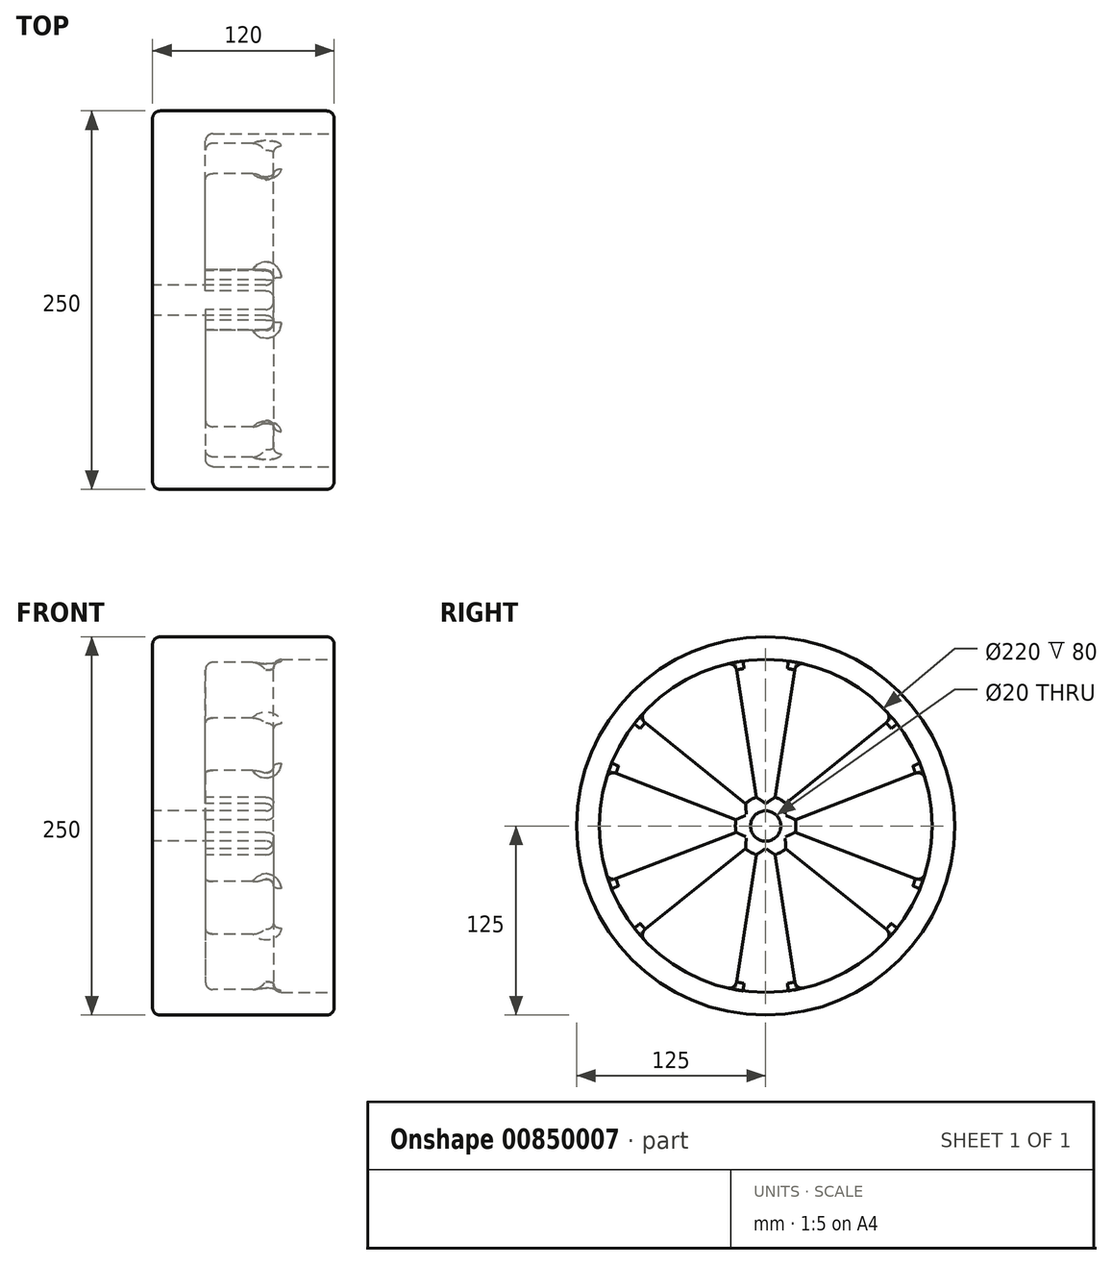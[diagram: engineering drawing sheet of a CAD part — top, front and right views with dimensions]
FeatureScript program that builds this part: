
annotation { "Feature Type Name" : "Feature", "Feature Type Description" : "" }
export const myFeature = defineFeature(function(context is Context, id is Id, definition is map)
    precondition{}
    {
        {
            var Q0;
            Q0=qCreatedBy(makeId("Right.planeOp"),FACE);
            var sketch = newSketch(context, id + "F0", { "sketchPlane" : qUnion([Q0])});
            skCircle(sketch, "E0", {"center": v(0, 0) * mm, "radius": 125 * mm});
            skSolve(sketch);
        }
        {
            var Q0;
            Q0=makeQuery(id+"F0.imprint","IMPRINT",FACE,{"disambiguationData":[TD([[makeQuery(id+"F0.imprint","IMPRINT",EDGE,{"derivedFrom":sQuery(id+"F0.wireOp",EDGE,"E0")}),1.0]])]});
            extrude(context, id + "F1", {"entities" : qUnion([Q0]), "depth" : 120 * mm, "offsetDistance" : 25 * mm});
        }
        {
            var Q0;
            Q0=makeQuery(id+"F1.opExtrude","CAP_FACE",FACE,{"disambiguationData":[OSD([sQuery(id+"F0.wireOp",EDGE,"E0")])],"isStart":false});
            var sketch = newSketch(context, id + "F2", { "sketchPlane" : qUnion([Q0])});
            skCircle(sketch, "E1", {"center": v(0, 0) * mm, "radius": 110 * mm});
            skSolve(sketch);
        }
        {
            var Q0;
            Q0=makeQuery(id+"F2.imprint","IMPRINT",FACE,{"disambiguationData":[TD([[makeQuery(id+"F2.imprint","IMPRINT",EDGE,{"derivedFrom":sQuery(id+"F2.wireOp",EDGE,"E1")}),1.0]])]});
            extrude(context, id + "F3", {"entities" : qUnion([Q0]), "operationType" : NewBodyOperationType.REMOVE, "oppositeDirection" : true, "depth" : 60 * mm, "offsetDistance" : 25 * mm});
        }
        {
            var Q0;
            Q0=makeQuery(id+"F3.boolean.opBoolean","COPY",FACE,{"derivedFrom":makeQuery(id+"F3.opExtrude","CAP_FACE",FACE,{"disambiguationData":[OSD([sQuery(id+"F2.wireOp",EDGE,"E1")])],"isStart":false})});
            var sketch = newSketch(context, id + "F4", { "sketchPlane" : qUnion([Q0])});
            skCircle(sketch, "E2", {"center": v(0, 0) * mm, "radius": 20 * mm});
            skCircle(sketch, "E3", {"center": v(0, 0) * mm, "radius": 10 * mm});
            skLineSegment(sketch, "E4", {"start": v(-6.24, 19) * mm, "end": v(-20, 108.17) * mm});
            skLineSegment(sketch, "E5", {"start": v(6.24, 19) * mm, "end": v(20, 108.17) * mm});
            skLineSegment(sketch, "E6.1.0", {"start": v(-13.33, 14.9) * mm, "end": v(-83.67, 71.4) * mm});
            skLineSegment(sketch, "E6.1.1", {"start": v(-19.58, 4.1) * mm, "end": v(-103.67, 36.76) * mm});
            skLineSegment(sketch, "E6.2.0", {"start": v(-19.58, -4.1) * mm, "end": v(-103.67, -36.76) * mm});
            skLineSegment(sketch, "E6.2.1", {"start": v(-13.33, -14.9) * mm, "end": v(-83.67, -71.4) * mm});
            skLineSegment(sketch, "E6.3.0", {"start": v(-6.24, -19) * mm, "end": v(-20, -108.17) * mm});
            skLineSegment(sketch, "E6.3.1", {"start": v(6.24, -19) * mm, "end": v(20, -108.17) * mm});
            skLineSegment(sketch, "E6.4.0", {"start": v(13.33, -14.9) * mm, "end": v(83.67, -71.4) * mm});
            skLineSegment(sketch, "E6.4.1", {"start": v(19.58, -4.1) * mm, "end": v(103.67, -36.76) * mm});
            skLineSegment(sketch, "E6.5.0", {"start": v(19.58, 4.1) * mm, "end": v(103.67, 36.76) * mm});
            skLineSegment(sketch, "E6.5.1", {"start": v(13.33, 14.9) * mm, "end": v(83.67, 71.4) * mm});
            skSolve(sketch);
        }
        {
            var Q0;
            {var subQ0=sQuery(id+"F4.wireOp",EDGE,"E4");Q0=makeQuery(id+"F4.imprint","IMPRINT",FACE,{"disambiguationData":[TD([[makeQuery(id+"F4.imprint","IMPRINT",EDGE,{"derivedFrom":subQ0}),-1.0]])]});}
            var Q1;
            Q1=makeQuery(id+"F4.imprint","IMPRINT",FACE,{"disambiguationData":[TD([[makeQuery(id+"F4.imprint","IMPRINT",EDGE,{"derivedFrom":sQuery(id+"F4.wireOp",EDGE,"E3")}),-1.0]])]});
            var Q2;
            {var subQ0=sQuery(id+"F4.wireOp",EDGE,"E6.5.0");Q2=makeQuery(id+"F4.imprint","IMPRINT",FACE,{"disambiguationData":[TD([[makeQuery(id+"F4.imprint","IMPRINT",EDGE,{"derivedFrom":subQ0}),1.0]])]});}
            var Q3;
            {var subQ0=sQuery(id+"F4.wireOp",EDGE,"E6.4.0");Q3=makeQuery(id+"F4.imprint","IMPRINT",FACE,{"disambiguationData":[TD([[makeQuery(id+"F4.imprint","IMPRINT",EDGE,{"derivedFrom":subQ0}),1.0]])]});}
            var Q4;
            {var subQ0=sQuery(id+"F4.wireOp",EDGE,"E6.3.0");Q4=makeQuery(id+"F4.imprint","IMPRINT",FACE,{"disambiguationData":[TD([[makeQuery(id+"F4.imprint","IMPRINT",EDGE,{"derivedFrom":subQ0}),1.0]])]});}
            var Q5;
            {var subQ0=sQuery(id+"F4.wireOp",EDGE,"E6.2.0");Q5=makeQuery(id+"F4.imprint","IMPRINT",FACE,{"disambiguationData":[TD([[makeQuery(id+"F4.imprint","IMPRINT",EDGE,{"derivedFrom":subQ0}),1.0]])]});}
            var Q6;
            {var subQ0=sQuery(id+"F4.wireOp",EDGE,"E6.1.0");Q6=makeQuery(id+"F4.imprint","IMPRINT",FACE,{"disambiguationData":[TD([[makeQuery(id+"F4.imprint","IMPRINT",EDGE,{"derivedFrom":subQ0}),1.0]])]});}
            extrude(context, id + "F5", {"entities" : qUnion([Q0, Q1, Q2, Q3, Q4, Q5, Q6]), "operationType" : NewBodyOperationType.ADD, "depth" : 20 * mm, "offsetDistance" : 25 * mm});
        }
        {
            var Q0;
            Q0=makeQuery(id+"F5.boolean.opBoolean","SPLIT",FACE,{"disambiguationData":[TD([makeQuery(id+"F5.opExtrude","SWEPT_FACE",FACE,{"disambiguationData":[OSD([sQuery(id+"F4.wireOp",EDGE,"E3")])]})])],"derivedFrom":makeQuery(id+"F3.boolean.opBoolean","COPY",FACE,{"derivedFrom":makeQuery(id+"F3.opExtrude","CAP_FACE",FACE,{"disambiguationData":[OSD([sQuery(id+"F2.wireOp",EDGE,"E1")])],"isStart":false})})});
            extrude(context, id + "F6", {"entities" : qUnion([Q0]), "operationType" : NewBodyOperationType.REMOVE, "oppositeDirection" : true, "depth" : 60 * mm, "offsetDistance" : 25 * mm});
        }
        {
            var Q0;
            {var subQ0=sQuery(id+"F2.wireOp",EDGE,"E1");var subQ1=sQuery(id+"F4.wireOp",EDGE,"E6.4.1");Q0=makeQuery(id+"F5.boolean.opBoolean","SPLIT",FACE,{"disambiguationData":[TD([makeQuery(id+"F5.opExtrude","SWEPT_FACE",FACE,{"disambiguationData":[OSD([subQ1])]})])],"derivedFrom":makeQuery(id+"F3.boolean.opBoolean","COPY",FACE,{"derivedFrom":makeQuery(id+"F3.opExtrude","CAP_FACE",FACE,{"disambiguationData":[OSD([subQ0])],"isStart":false})})});}
            var Q1;
            {var subQ0=sQuery(id+"F2.wireOp",EDGE,"E1");var subQ1=sQuery(id+"F4.wireOp",EDGE,"E5");Q1=makeQuery(id+"F5.boolean.opBoolean","SPLIT",FACE,{"disambiguationData":[TD([makeQuery(id+"F5.opExtrude","SWEPT_FACE",FACE,{"disambiguationData":[OSD([subQ1])]})])],"derivedFrom":makeQuery(id+"F3.boolean.opBoolean","COPY",FACE,{"derivedFrom":makeQuery(id+"F3.opExtrude","CAP_FACE",FACE,{"disambiguationData":[OSD([subQ0])],"isStart":false})})});}
            var Q2;
            {var subQ0=sQuery(id+"F2.wireOp",EDGE,"E1");var subQ1=sQuery(id+"F4.wireOp",EDGE,"E4");Q2=makeQuery(id+"F5.boolean.opBoolean","SPLIT",FACE,{"disambiguationData":[TD([makeQuery(id+"F5.opExtrude","SWEPT_FACE",FACE,{"disambiguationData":[OSD([subQ1])]})])],"derivedFrom":makeQuery(id+"F3.boolean.opBoolean","COPY",FACE,{"derivedFrom":makeQuery(id+"F3.opExtrude","CAP_FACE",FACE,{"disambiguationData":[OSD([subQ0])],"isStart":false})})});}
            var Q3;
            {var subQ0=sQuery(id+"F2.wireOp",EDGE,"E1");var subQ1=sQuery(id+"F4.wireOp",EDGE,"E6.1.1");Q3=makeQuery(id+"F5.boolean.opBoolean","SPLIT",FACE,{"disambiguationData":[TD([makeQuery(id+"F5.opExtrude","SWEPT_FACE",FACE,{"disambiguationData":[OSD([subQ1])]})])],"derivedFrom":makeQuery(id+"F3.boolean.opBoolean","COPY",FACE,{"derivedFrom":makeQuery(id+"F3.opExtrude","CAP_FACE",FACE,{"disambiguationData":[OSD([subQ0])],"isStart":false})})});}
            var Q4;
            {var subQ0=sQuery(id+"F2.wireOp",EDGE,"E1");var subQ1=sQuery(id+"F4.wireOp",EDGE,"E6.2.1");Q4=makeQuery(id+"F5.boolean.opBoolean","SPLIT",FACE,{"disambiguationData":[TD([makeQuery(id+"F5.opExtrude","SWEPT_FACE",FACE,{"disambiguationData":[OSD([subQ1])]})])],"derivedFrom":makeQuery(id+"F3.boolean.opBoolean","COPY",FACE,{"derivedFrom":makeQuery(id+"F3.opExtrude","CAP_FACE",FACE,{"disambiguationData":[OSD([subQ0])],"isStart":false})})});}
            var Q5;
            {var subQ0=sQuery(id+"F2.wireOp",EDGE,"E1");var subQ2=sQuery(id+"F4.wireOp",EDGE,"E6.3.1");Q5=makeQuery(id+"F5.boolean.opBoolean","SPLIT",FACE,{"disambiguationData":[TD([makeQuery(id+"F5.opExtrude","SWEPT_FACE",FACE,{"disambiguationData":[OSD([subQ2])]})])],"derivedFrom":makeQuery(id+"F3.boolean.opBoolean","COPY",FACE,{"derivedFrom":makeQuery(id+"F3.opExtrude","CAP_FACE",FACE,{"disambiguationData":[OSD([subQ0])],"isStart":false})})});}
            extrude(context, id + "F7", {"entities" : qUnion([Q0, Q1, Q2, Q3, Q4, Q5]), "operationType" : NewBodyOperationType.REMOVE, "oppositeDirection" : true, "depth" : 25 * mm, "offsetDistance" : 25 * mm});
        }
        {
            var Q0;
            Q0=makeQuery(id+"F3.boolean.opBoolean","COPY",EDGE,{"derivedFrom":makeQuery(id+"F3.opExtrude","CAP_EDGE",EDGE,{"disambiguationData":[OSD([sQuery(id+"F2.wireOp",EDGE,"E1")])],"isStart":true})});
            var Q1;
            Q1=makeQuery(id+"F1.opExtrude","CAP_EDGE",EDGE,{"disambiguationData":[OSD([sQuery(id+"F0.wireOp",EDGE,"E0")])],"isStart":false});
            var Q2;
            Q2=makeQuery(id+"F5.opExtrude","CAP_EDGE",EDGE,{"disambiguationData":[OSD([sQuery(id+"F4.wireOp",EDGE,"E6.1.1")])],"isStart":false});
            var Q3;
            Q3=makeQuery(id+"F5.opExtrude","CAP_EDGE",EDGE,{"disambiguationData":[OSD([sQuery(id+"F4.wireOp",EDGE,"E6.1.0")])],"isStart":false});
            var Q4;
            Q4=makeQuery(id+"F5.opExtrude","CAP_EDGE",EDGE,{"disambiguationData":[OSD([sQuery(id+"F4.wireOp",EDGE,"E4")])],"isStart":false});
            var Q5;
            Q5=makeQuery(id+"F5.opExtrude","CAP_EDGE",EDGE,{"disambiguationData":[OSD([sQuery(id+"F4.wireOp",EDGE,"E5")])],"isStart":false});
            var Q6;
            Q6=makeQuery(id+"F5.opExtrude","CAP_EDGE",EDGE,{"disambiguationData":[OSD([sQuery(id+"F4.wireOp",EDGE,"E6.5.1")])],"isStart":false});
            var Q7;
            Q7=makeQuery(id+"F5.opExtrude","CAP_EDGE",EDGE,{"disambiguationData":[OSD([sQuery(id+"F4.wireOp",EDGE,"E6.4.1")])],"isStart":false});
            var Q8;
            Q8=makeQuery(id+"F5.opExtrude","CAP_EDGE",EDGE,{"disambiguationData":[OSD([sQuery(id+"F4.wireOp",EDGE,"E6.4.0")])],"isStart":false});
            var Q9;
            Q9=makeQuery(id+"F5.opExtrude","CAP_EDGE",EDGE,{"disambiguationData":[OSD([sQuery(id+"F4.wireOp",EDGE,"E6.3.0")])],"isStart":false});
            var Q10;
            Q10=makeQuery(id+"F5.opExtrude","CAP_EDGE",EDGE,{"disambiguationData":[OSD([sQuery(id+"F4.wireOp",EDGE,"E6.2.0")])],"isStart":false});
            var Q11;
            Q11=makeQuery(id+"F5.opExtrude","CAP_EDGE",EDGE,{"disambiguationData":[OSD([sQuery(id+"F4.wireOp",EDGE,"E6.2.1")])],"isStart":false});
            var Q12;
            Q12=makeQuery(id+"F5.opExtrude","CAP_EDGE",EDGE,{"disambiguationData":[OSD([sQuery(id+"F4.wireOp",EDGE,"E6.3.1")])],"isStart":false});
            var Q13;
            Q13=makeQuery(id+"F5.opExtrude","CAP_EDGE",EDGE,{"disambiguationData":[OSD([sQuery(id+"F4.wireOp",EDGE,"E6.5.0")])],"isStart":false});
            var Q14;
            {var subQ0=sQuery(id+"F2.wireOp",EDGE,"E1");Q14=makeQuery(id+"F7.boolean.opBoolean","COPY",EDGE,{"derivedFrom":makeQuery(id+"F7.opExtrude","CAP_EDGE",EDGE,{"disambiguationData":[OSD([subQ0]),TDD([makeQuery(id+"F5.boolean.opBoolean","SPLIT",EDGE,{"disambiguationData":[TD([makeQuery(id+"F5.opExtrude","SWEPT_FACE",FACE,{"disambiguationData":[OSD([sQuery(id+"F4.wireOp",EDGE,"E6.1.1")])]})])],"derivedFrom":makeQuery(id+"F3.boolean.opBoolean","COPY",EDGE,{"derivedFrom":makeQuery(id+"F3.opExtrude","CAP_EDGE",EDGE,{"disambiguationData":[OSD([subQ0])],"isStart":false})})})])],"isStart":false})});}
            var Q15;
            {var subQ0=sQuery(id+"F2.wireOp",EDGE,"E1");Q15=makeQuery(id+"F7.boolean.opBoolean","COPY",EDGE,{"derivedFrom":makeQuery(id+"F7.opExtrude","CAP_EDGE",EDGE,{"disambiguationData":[OSD([subQ0]),TDD([makeQuery(id+"F5.boolean.opBoolean","SPLIT",EDGE,{"disambiguationData":[TD([makeQuery(id+"F5.opExtrude","SWEPT_FACE",FACE,{"disambiguationData":[OSD([sQuery(id+"F4.wireOp",EDGE,"E4")])]})])],"derivedFrom":makeQuery(id+"F3.boolean.opBoolean","COPY",EDGE,{"derivedFrom":makeQuery(id+"F3.opExtrude","CAP_EDGE",EDGE,{"disambiguationData":[OSD([subQ0])],"isStart":false})})})])],"isStart":false})});}
            var Q16;
            {var subQ0=sQuery(id+"F2.wireOp",EDGE,"E1");Q16=makeQuery(id+"F7.boolean.opBoolean","COPY",EDGE,{"derivedFrom":makeQuery(id+"F7.opExtrude","CAP_EDGE",EDGE,{"disambiguationData":[OSD([subQ0]),TDD([makeQuery(id+"F5.boolean.opBoolean","SPLIT",EDGE,{"disambiguationData":[TD([makeQuery(id+"F5.opExtrude","SWEPT_FACE",FACE,{"disambiguationData":[OSD([sQuery(id+"F4.wireOp",EDGE,"E5")])]})])],"derivedFrom":makeQuery(id+"F3.boolean.opBoolean","COPY",EDGE,{"derivedFrom":makeQuery(id+"F3.opExtrude","CAP_EDGE",EDGE,{"disambiguationData":[OSD([subQ0])],"isStart":false})})})])],"isStart":false})});}
            var Q17;
            {var subQ0=sQuery(id+"F2.wireOp",EDGE,"E1");Q17=makeQuery(id+"F7.boolean.opBoolean","COPY",EDGE,{"derivedFrom":makeQuery(id+"F7.opExtrude","CAP_EDGE",EDGE,{"disambiguationData":[OSD([subQ0]),TDD([makeQuery(id+"F5.boolean.opBoolean","SPLIT",EDGE,{"disambiguationData":[TD([makeQuery(id+"F5.opExtrude","SWEPT_FACE",FACE,{"disambiguationData":[OSD([sQuery(id+"F4.wireOp",EDGE,"E6.4.1")])]})])],"derivedFrom":makeQuery(id+"F3.boolean.opBoolean","COPY",EDGE,{"derivedFrom":makeQuery(id+"F3.opExtrude","CAP_EDGE",EDGE,{"disambiguationData":[OSD([subQ0])],"isStart":false})})})])],"isStart":false})});}
            var Q18;
            Q18=makeQuery(id+"F5.opExtrude","CAP_FACE",FACE,{"disambiguationData":[OSD([sQuery(id+"F2.wireOp",EDGE,"E1"),sQuery(id+"F4.wireOp",EDGE,"E2"),sQuery(id+"F4.wireOp",EDGE,"E3"),sQuery(id+"F4.wireOp",EDGE,"E4"),sQuery(id+"F4.wireOp",EDGE,"E5"),sQuery(id+"F4.wireOp",EDGE,"E6.1.0"),sQuery(id+"F4.wireOp",EDGE,"E6.1.1"),sQuery(id+"F4.wireOp",EDGE,"E6.2.0"),sQuery(id+"F4.wireOp",EDGE,"E6.2.1"),sQuery(id+"F4.wireOp",EDGE,"E6.3.0"),sQuery(id+"F4.wireOp",EDGE,"E6.3.1"),sQuery(id+"F4.wireOp",EDGE,"E6.4.0"),sQuery(id+"F4.wireOp",EDGE,"E6.4.1"),sQuery(id+"F4.wireOp",EDGE,"E6.5.0"),sQuery(id+"F4.wireOp",EDGE,"E6.5.1")])],"isStart":false});
            var Q19;
            {var subQ0=sQuery(id+"F2.wireOp",EDGE,"E1");Q19=makeQuery(id+"F7.boolean.opBoolean","COPY",EDGE,{"derivedFrom":makeQuery(id+"F7.opExtrude","CAP_EDGE",EDGE,{"disambiguationData":[OSD([subQ0]),TDD([makeQuery(id+"F5.boolean.opBoolean","SPLIT",EDGE,{"disambiguationData":[TD([makeQuery(id+"F5.opExtrude","SWEPT_FACE",FACE,{"disambiguationData":[OSD([sQuery(id+"F4.wireOp",EDGE,"E6.3.1")])]})])],"derivedFrom":makeQuery(id+"F3.boolean.opBoolean","COPY",EDGE,{"derivedFrom":makeQuery(id+"F3.opExtrude","CAP_EDGE",EDGE,{"disambiguationData":[OSD([subQ0])],"isStart":false})})})])],"isStart":false})});}
            var Q20;
            {var subQ0=sQuery(id+"F2.wireOp",EDGE,"E1");Q20=makeQuery(id+"F7.boolean.opBoolean","COPY",EDGE,{"derivedFrom":makeQuery(id+"F7.opExtrude","CAP_EDGE",EDGE,{"disambiguationData":[OSD([subQ0]),TDD([makeQuery(id+"F5.boolean.opBoolean","SPLIT",EDGE,{"disambiguationData":[TD([makeQuery(id+"F5.opExtrude","SWEPT_FACE",FACE,{"disambiguationData":[OSD([sQuery(id+"F4.wireOp",EDGE,"E6.2.1")])]})])],"derivedFrom":makeQuery(id+"F3.boolean.opBoolean","COPY",EDGE,{"derivedFrom":makeQuery(id+"F3.opExtrude","CAP_EDGE",EDGE,{"disambiguationData":[OSD([subQ0])],"isStart":false})})})])],"isStart":false})});}
            var Q21;
            Q21=makeQuery(id+"F1.opExtrude","CAP_EDGE",EDGE,{"disambiguationData":[OSD([sQuery(id+"F0.wireOp",EDGE,"E0")])],"isStart":true});
            fillet(context, id + "F8", {"entities" : qUnion([Q0, Q1, Q2, Q3, Q4, Q5, Q6, Q7, Q8, Q9, Q10, Q11, Q12, Q13, Q14, Q15, Q16, Q17, Q18, Q19, Q20, Q21]), "radius" : 5 * mm, "tangentPropagation" : true, "allowEdgeOverflow" : false});
        }
    });
